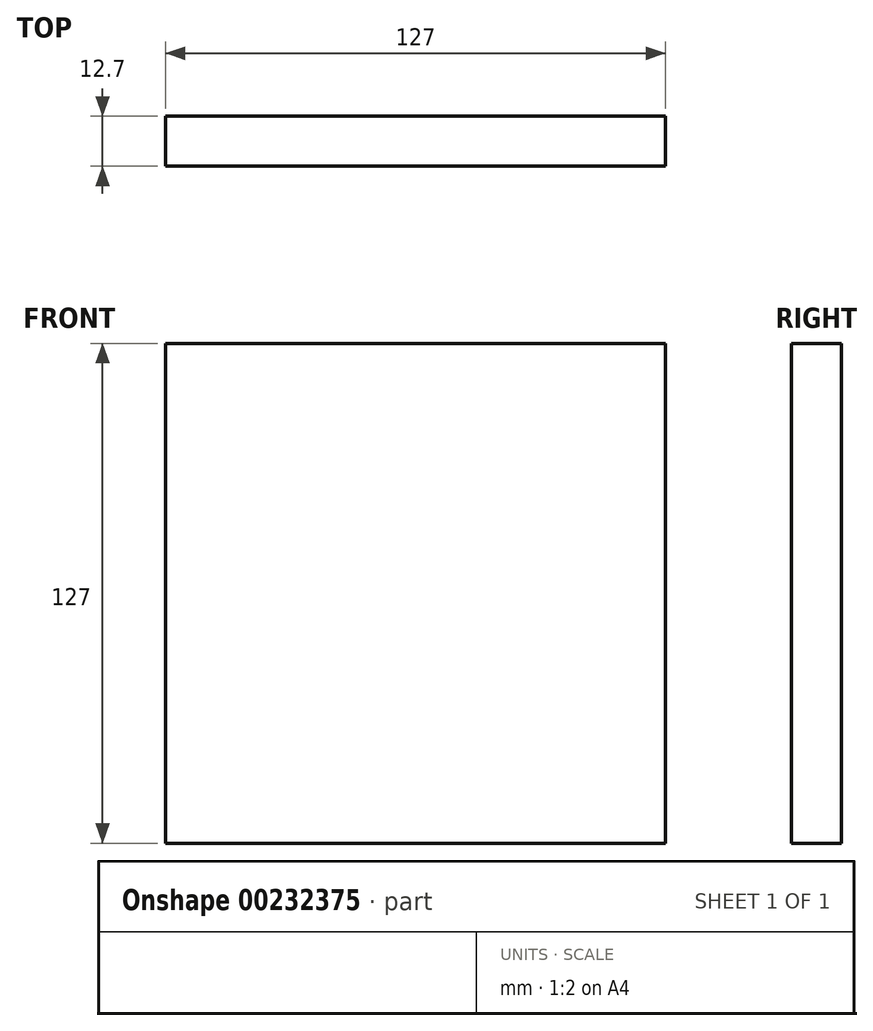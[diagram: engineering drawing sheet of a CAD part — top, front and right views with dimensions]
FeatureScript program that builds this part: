
annotation { "Feature Type Name" : "Feature", "Feature Type Description" : "" }
export const myFeature = defineFeature(function(context is Context, id is Id, definition is map)
    precondition{}
    {
        {
            var Q0;
            Q0=qCreatedBy(makeId("Front.planeOp"),FACE);
            var sketch = newSketch(context, id + "F0", { "sketchPlane" : qUnion([Q0])});
            skLineSegment(sketch, "E0.bottom", {"start": v(-7.6, -94.2) * mm, "end": v(119.4, -94.2) * mm});
            skLineSegment(sketch, "E0.top", {"start": v(-7.6, 32.8) * mm, "end": v(119.4, 32.8) * mm});
            skLineSegment(sketch, "E0.left", {"start": v(119.4, 32.8) * mm, "end": v(119.4, -94.2) * mm});
            skLineSegment(sketch, "E0.right", {"start": v(-7.6, 32.8) * mm, "end": v(-7.6, -94.2) * mm});
            skSolve(sketch);
        }
        {
            var Q0;
            Q0 = qSketchRegion(id + "F0", true);
            extrude(context, id + "F1", {"entities" : qUnion([Q0]), "depth" : 12.7 * mm});
        }
    });
